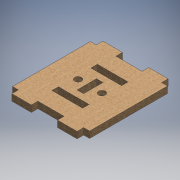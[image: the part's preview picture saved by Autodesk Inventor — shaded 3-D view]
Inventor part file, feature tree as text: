
AUTODESK INVENTOR PART (.ipt)
format: ipt  version: 2016 (Build 200138000, 138)  size: 179,712 bytes
history: native  units: mm
features: extrude x1, sketch x1
ambient origin geometry x8: Origin, YZ Plane, XZ Plane, XY Plane, X Axis, Y Axis, Z Axis, Center Point
bodies: Body1 (feature_tree)
feature tree (2):
  extrude  "Extrusion4"  Depth=75.835317mm
  sketch  "Sketch1"  dims[d0=75.0mm d1=75.835317mm d2=18.958829mm d3=6.39mm d4=12.78mm d21=6.39mm d22=29.89mm d24=18.958829mm d25=6.39mm d30=37.917659mm d41=6.6675mm d42=6.39mm d43=0.0mm]
